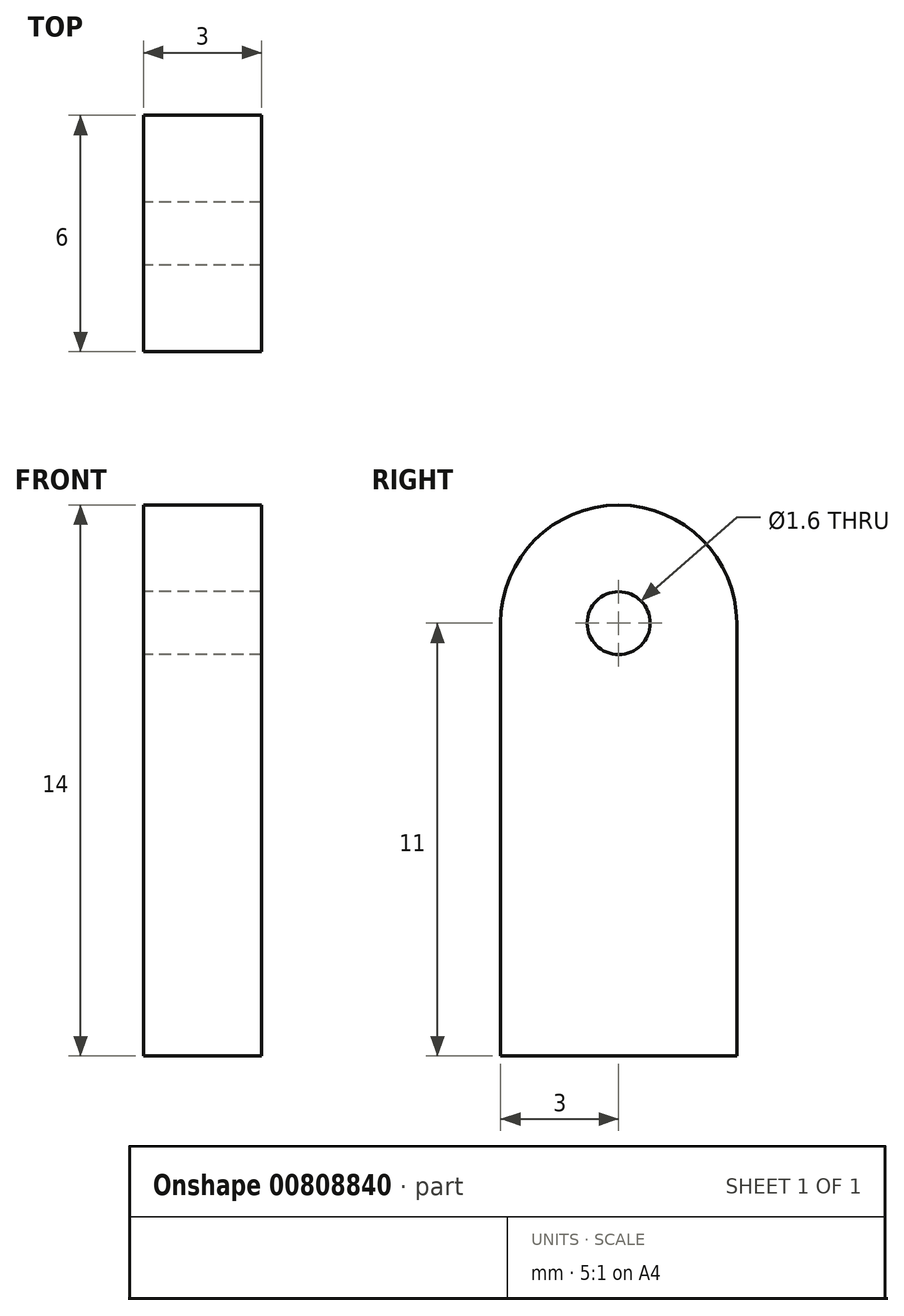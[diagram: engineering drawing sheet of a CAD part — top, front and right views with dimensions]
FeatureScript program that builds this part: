
annotation { "Feature Type Name" : "Feature", "Feature Type Description" : "" }
export const myFeature = defineFeature(function(context is Context, id is Id, definition is map)
    precondition{}
    {
        {
            var Q0;
            Q0=qCreatedBy(makeId("Right.planeOp"),FACE);
            var sketch = newSketch(context, id + "F0", { "sketchPlane" : qUnion([Q0])});
            skLineSegment(sketch, "E0.bottom", {"start": v(0, 7) * mm, "end": v(0, 7) * mm});
            skLineSegment(sketch, "E0.top", {"start": v(-3, -7) * mm, "end": v(3, -7) * mm});
            skLineSegment(sketch, "E0.left", {"start": v(-3, 4) * mm, "end": v(-3, -7) * mm});
            skLineSegment(sketch, "E0.right", {"start": v(3, 4) * mm, "end": v(3, -7) * mm});
            skPoint(sketch, "E0.middle", {"position": v(0, 0) * mm});
            skCircle(sketch, "E1", {"center": v(0, 4) * mm, "radius": 0.8 * mm});
            skPoint(sketch, "E2.visualSharp", {"position": v(3, 7) * mm});
            skArc(sketch, "E2.filletArc", {"start": v(3, 4) * mm, "mid": v(2.12, 6.12) * mm, "end": v(0, 7) * mm});
            skPoint(sketch, "E3.visualSharp", {"position": v(-3, 7) * mm});
            skArc(sketch, "E3.filletArc", {"start": v(0, 7) * mm, "mid": v(-2.12, 6.12) * mm, "end": v(-3, 4) * mm});
            skSolve(sketch);
        }
        {
            var Q0;
            Q0=qSketchRegion(id+"F0",true);
            extrude(context, id + "F1", {"entities" : qUnion([Q0]), "depth" : 3 * mm, "offsetDistance" : 25 * mm});
        }
    });
